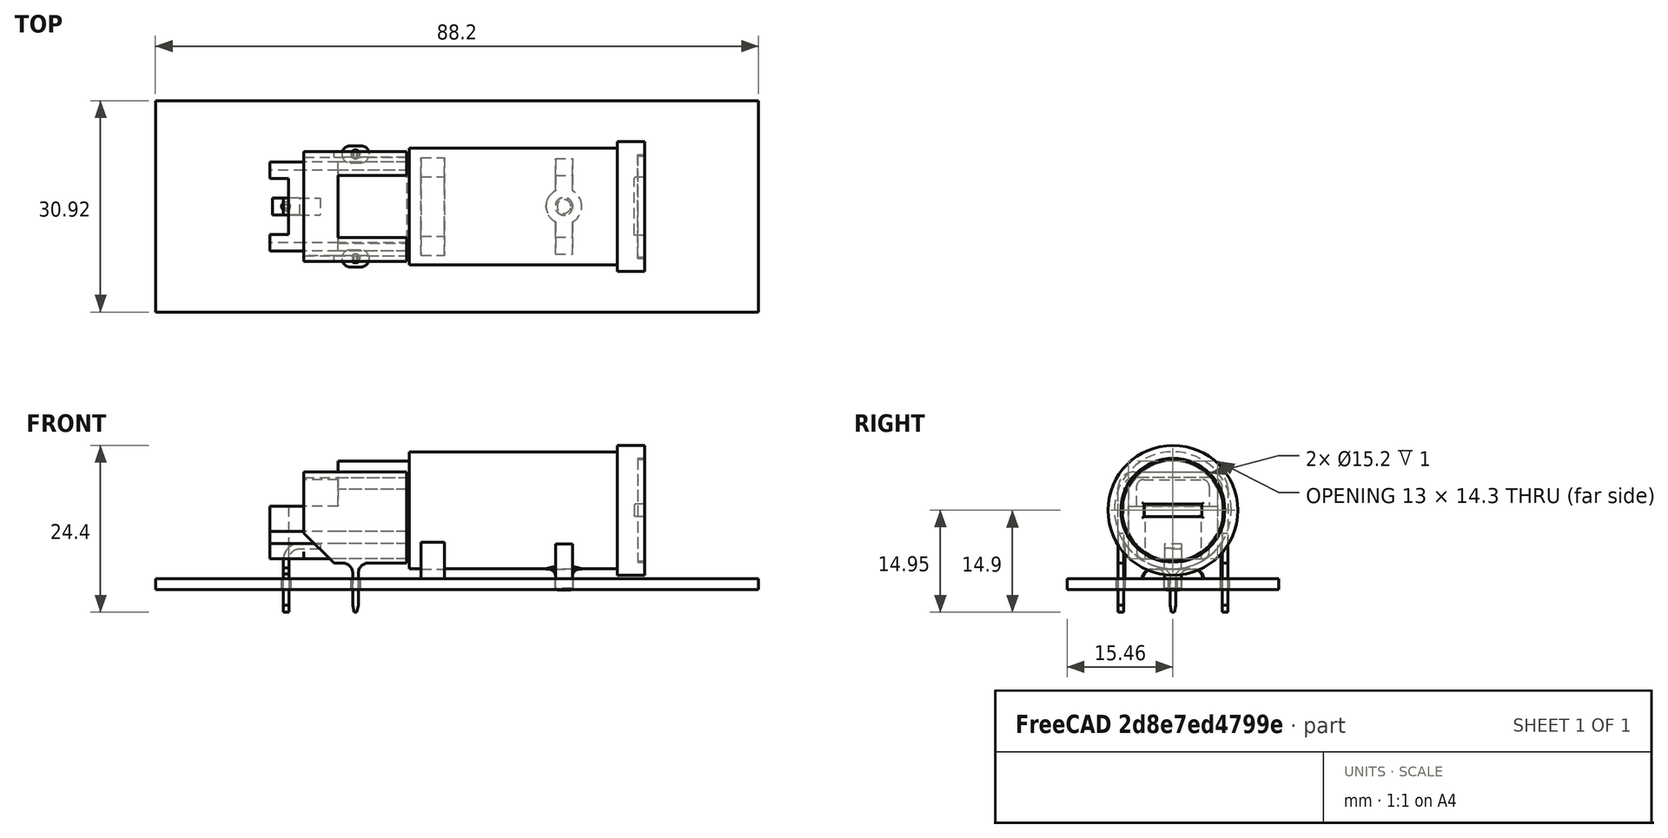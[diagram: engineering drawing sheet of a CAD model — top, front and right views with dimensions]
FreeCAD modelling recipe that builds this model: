
FCSTD DOCUMENT  (FreeCAD 0.17R12320 (Git))
Label: Fuseholder_Cylinder-5x20mm-or-6.3x32mm_Schurter_FUP_0031.25x0_Horizontal_Closed
License: All rights reserved
LicenseURL: http://en.wikipedia.org/wiki/All_rights_reserved
objects: Sketcher::SketchObject×16, PartDesign::Pad×9, PartDesign::Pocket×5, Part::FeaturePython×5, PartDesign::Plane×4, PartDesign::Fillet×3, PartDesign::Body×3, PartDesign::Revolution×1, PartDesign::Chamfer×1, PartDesign::ShapeBinder×1, Part::MultiFuse×1, App::DocumentObjectGroup×1
note: 64 computed .brp shape members not serialized (recipe doc carries the construction recipe); baked Part::Feature solids carry a one-line shape summary decoded from their .brp

FEATURE [Sketcher::SketchObject] Sketch
  MapMode = 5
  Placement = pos=(0,0,0) rot=(1,0,0;1.5708rad)
  Support = -> [XZ_Plane]
  expr: Constraints[9] = 11.77 + 30.48 + 10.16
  sketch-geometry (5):
    g0: LineSegment [constr] StartX=-2.39 StartY=19.5 StartZ=0 EndX=52.41 EndY=19.5 EndZ=0
    g1: LineSegment [constr] StartX=52.41 StartY=19.5 StartZ=0 EndX=52.41 EndY=0.5 EndZ=0
    g2: LineSegment [constr] StartX=52.41 StartY=0.5 StartZ=0 EndX=-2.39 EndY=0.5 EndZ=0
    g3: LineSegment [constr] StartX=-2.39 StartY=0.5 StartZ=0 EndX=-2.39 EndY=19.5 EndZ=0
    g4: LineSegment StartX=52.41 StartY=10 StartZ=0 EndX=-2.39 EndY=10 EndZ=0
  constraints (16):
    c: Coincident(g0,g1)
    c: Coincident(g1,g2)
    c: Coincident(g2,g3)
    c: Coincident(g3,g0)
    c: Horizontal(g0)
    c: Horizontal(g2)
    c: Vertical(g1)
    c: Vertical(g3)
    c: DistanceX(g0,g0) = 54.8
    c: DistanceX(g-1,g1) = 52.41
    c: DistanceY(g3,g3) = 19
    c: PointOnObject(g4,g1)
    c: PointOnObject(g4,g3)
    c: Horizontal(g4)
    c: Symmetric(g1,g0,g4)
    c: DistanceY(g-1,g0) = 19.5
FEATURE [Sketcher::SketchObject] Sketch001
  ExternalGeometry = -> [Sketch]
  MapMode = 5
  Placement = pos=(0,0,0) rot=(1,0,0;1.5708rad)
  Support = -> [XZ_Plane]
  sketch-geometry (11):
    g0: LineSegment StartX=52.41 StartY=10 StartZ=0 EndX=52.41 EndY=19.5 EndZ=0
    g1: LineSegment StartX=52.41 StartY=19.5 StartZ=0 EndX=48.41 EndY=19.5 EndZ=0
    g2: LineSegment StartX=48.41 StartY=19.5 StartZ=0 EndX=48.41 EndY=18.55 EndZ=0
    g3: LineSegment StartX=48.41 StartY=18.55 StartZ=0 EndX=18.01 EndY=18.55 EndZ=0
    g4: LineSegment StartX=18.01 StartY=18.55 StartZ=0 EndX=18.01 EndY=10 EndZ=0
    g5: LineSegment StartX=18.01 StartY=10 StartZ=0 EndX=52.41 EndY=10 EndZ=0
    g6: LineSegment [constr] StartX=52.41 StartY=10 StartZ=0 EndX=52.41 EndY=0.5 EndZ=0
    g7: LineSegment [constr] StartX=52.41 StartY=0.5 StartZ=0 EndX=48.41 EndY=0.5 EndZ=0
    g8: LineSegment [constr] StartX=48.41 StartY=0.5 StartZ=0 EndX=48.41 EndY=1.45 EndZ=0
    g9: LineSegment [constr] StartX=48.41 StartY=1.45 StartZ=0 EndX=18.01 EndY=1.45 EndZ=0
    g10: LineSegment [constr] StartX=18.01 StartY=1.45 StartZ=0 EndX=18.01 EndY=10 EndZ=0
  constraints (30):
    c: Coincident(g-3,g0)
    c: Vertical(g0)
    c: Coincident(g0,g1)
    c: Horizontal(g1)
    c: Coincident(g1,g2)
    c: Vertical(g2)
    c: Coincident(g2,g3)
    c: Horizontal(g3)
    c: Coincident(g3,g4)
    c: PointOnObject(g5,g-3)
    c: Coincident(g5,g0)
    c: DistanceX(g3,g3) = 30.4
    c: Vertical(g4)
    c: DistanceX(g1,g1) = 4
    c: Coincident(g0,g6)
    c: Vertical(g6)
    c: Coincident(g6,g7)
    c: Horizontal(g7)
    c: Coincident(g7,g8)
    c: Vertical(g8)
    c: Coincident(g8,g9)
    c: Horizontal(g9)
    c: Coincident(g9,g10)
    c: Vertical(g10)
    c: Symmetric(g8,g2,g-3)
    c: Symmetric(g0,g6,g-3)
    c: DistanceY(g6,g0) = 19
    c: Coincident(g5,g4)
    c: DistanceY(g9,g3) = 17.1
    c: Coincident(g10,g4)
FEATURE [PartDesign::Revolution] Revolution
  Angle = 360
  Axis = (-1,0,0)
  Base = (52.41,0,10)
  Placement = pos=(0,0,0) rot=(1,0,0;1.5708rad)
  Profile = -> Sketch001
  ReferenceAxis = -> Sketch [Edge1]
  Reversed = true
FEATURE [Sketcher::SketchObject] Sketch002
  ExternalGeometry = -> [Revolution]
  MapMode = 5
  Placement = pos=(18.01,0,0) rot=(0.707107,0,-0.707107;3.14159rad)
  Support = -> [Revolution]
  sketch-geometry (13):
    g0: Circle [constr] CenterX=-10 CenterY=0 CenterZ=0 NormalX=0 NormalY=0 NormalZ=1 AngleXU=0 Radius=7.2
    g1: GeomPoint [constr] X=-18.55 Y=0 Z=0
    g2: GeomPoint [constr] X=-17.2 Y=0 Z=0
    g3: LineSegment StartX=-13.0968 StartY=6.5 StartZ=0 EndX=-6.90323 EndY=6.5 EndZ=0
    g4: LineSegment StartX=-13.0968 StartY=-6.5 StartZ=0 EndX=-6.90323 EndY=-6.5 EndZ=0
    g5: LineSegment StartX=-5.1266 StartY=5.3 StartZ=0 EndX=-3.9 EndY=5.3 EndZ=0
    g6: LineSegment StartX=-2.9 StartY=4.3 StartZ=0 EndX=-2.9 EndY=-4.3 EndZ=0
    g7: LineSegment StartX=-3.9 StartY=-5.3 StartZ=0 EndX=-5.1266 EndY=-5.3 EndZ=0
    g8: ArcOfCircle CenterX=-3.9 CenterY=4.3 CenterZ=0 NormalX=0 NormalY=0 NormalZ=1 AngleXU=0 Radius=1 StartAngle=0 EndAngle=1.5708
    g9: ArcOfCircle CenterX=-3.9 CenterY=-4.3 CenterZ=0 NormalX=0 NormalY=0 NormalZ=1 AngleXU=0 Radius=1 StartAngle=4.71239 EndAngle=6.28319
    g10: ArcOfCircle CenterX=-10 CenterY=0 CenterZ=0 NormalX=0 NormalY=0 NormalZ=1 AngleXU=0 Radius=7.2 StartAngle=2.01541 EndAngle=4.26778
    g11: ArcOfCircle CenterX=-10 CenterY=0 CenterZ=0 NormalX=0 NormalY=0 NormalZ=1 AngleXU=0 Radius=7.2 StartAngle=0.827307 EndAngle=1.12618
    g12: ArcOfCircle CenterX=-10 CenterY=0 CenterZ=0 NormalX=0 NormalY=0 NormalZ=1 AngleXU=0 Radius=7.2 StartAngle=5.157 EndAngle=5.45588
  constraints (38):
    c: Coincident(g0,g-3)
    c: PointOnObject(g1,g-3)
    c: PointOnObject(g2,g0)
    c: PointOnObject(g2,g-1)
    c: PointOnObject(g1,g-1)
    c: DistanceX(g1,g2) = 1.35
    c: PointOnObject(g3,g0)
    c: Horizontal(g3)
    c: PointOnObject(g4,g0)
    c: Horizontal(g4)
    c: Symmetric(g3,g4,g-1)
    c: DistanceY(g4,g3) = 13
    c: PointOnObject(g3,g0)
    c: DistanceX(g3,g3) = 6.19355
    c: PointOnObject(g4,g0)
    c: PointOnObject(g5,g0)
    c: Horizontal(g5)
    c: Vertical(g6)
    c: PointOnObject(g7,g0)
    c: Horizontal(g7)
    c: Symmetric(g5,g7,g-1)
    c: DistanceY(g7,g5) = 10.6
    c: Tangent(g6,g8) = 1.5708
    c: Tangent(g5,g8) = 1.5708
    c: Tangent(g6,g9) = 1.5708
    c: Tangent(g7,g9) = 1.5708
    c: Radius(g8) = 1
    c: Equal(g8,g9)
    c: Coincident(g10,g0)
    c: Coincident(g10,g3)
    c: Coincident(g10,g4)
    c: Coincident(g11,g0)
    c: Coincident(g11,g3)
    c: Coincident(g11,g5)
    c: Coincident(g12,g0)
    c: Coincident(g12,g4)
    c: Coincident(g12,g7)
    c: DistanceX(g6,g-1) = 2.9
FEATURE [PartDesign::Pad] Pad
  BaseFeature = -> Revolution
  Length = 10.4
  Length2 = 100
  Placement = pos=(0,0,0) rot=(1,0,0;1.5708rad)
  Profile = -> Sketch002
  Type = 0
FEATURE [Sketcher::SketchObject] Sketch003
  ExternalGeometry = -> [Pad]
  MapMode = 5
  Placement = pos=(7.61,0,0) rot=(0.707107,0,-0.707107;3.14159rad)
  Support = -> [Pad]
  sketch-geometry (16):
    g0: LineSegment StartX=-2.9 StartY=4.3 StartZ=0 EndX=-2.9 EndY=-4.3 EndZ=0
    g1: LineSegment StartX=-3.9 StartY=5.3 StartZ=0 EndX=-5.1266 EndY=5.3 EndZ=0
    g2: LineSegment StartX=-5.1266 StartY=-5.3 StartZ=0 EndX=-3.9 EndY=-5.3 EndZ=0
    g3: LineSegment StartX=-6.90323 StartY=6.5 StartZ=0 EndX=-10.5968 EndY=6.5 EndZ=0
    g4: LineSegment StartX=-10.5968 StartY=-6.5 StartZ=0 EndX=-6.90323 EndY=-6.5 EndZ=0
    g5: ArcOfCircle CenterX=-10 CenterY=0 CenterZ=0 NormalX=0 NormalY=0 NormalZ=1 AngleXU=0 Radius=7.2 StartAngle=0.827307 EndAngle=1.12618
    g6: ArcOfCircle CenterX=-10 CenterY=0 CenterZ=0 NormalX=0 NormalY=0 NormalZ=1 AngleXU=0 Radius=7.2 StartAngle=5.157 EndAngle=5.45588
    g7: LineSegment StartX=-10.5968 StartY=6.5 StartZ=0 EndX=-10.5968 EndY=5.3 EndZ=0
    g8: LineSegment StartX=-10.5968 StartY=5.3 StartZ=0 EndX=-13.4968 EndY=5.3 EndZ=0
    g9: LineSegment StartX=-14.4968 StartY=4.3 StartZ=0 EndX=-14.4968 EndY=-4.3 EndZ=0
    g10: LineSegment StartX=-13.4968 StartY=-5.3 StartZ=0 EndX=-10.5968 EndY=-5.3 EndZ=0
    g11: LineSegment StartX=-10.5968 StartY=-5.3 StartZ=0 EndX=-10.5968 EndY=-6.5 EndZ=0
    g12: ArcOfCircle CenterX=-13.4968 CenterY=-4.3 CenterZ=0 NormalX=0 NormalY=0 NormalZ=1 AngleXU=0 Radius=1 StartAngle=3.14159 EndAngle=4.71239
    g13: ArcOfCircle CenterX=-13.4968 CenterY=4.3 CenterZ=0 NormalX=0 NormalY=0 NormalZ=1 AngleXU=0 Radius=1 StartAngle=1.5708 EndAngle=3.14159
    g14: ArcOfCircle CenterX=-3.9 CenterY=4.3 CenterZ=0 NormalX=0 NormalY=0 NormalZ=1 AngleXU=0 Radius=1 StartAngle=9e-12 EndAngle=1.5708
    g15: ArcOfCircle CenterX=-3.9 CenterY=-4.3 CenterZ=0 NormalX=0 NormalY=0 NormalZ=1 AngleXU=0 Radius=1 StartAngle=4.71239 EndAngle=6.28319
  constraints (41):
    c: Coincident(g0,g-8)
    c: Coincident(g0,g-8)
    c: Coincident(g1,g-7)
    c: Coincident(g1,g-7)
    c: Coincident(g2,g-6)
    c: Coincident(g2,g-6)
    c: Coincident(g-4,g3)
    c: PointOnObject(g3,g-4)
    c: Coincident(g4,g-5)
    c: Coincident(g5,g-3)
    c: Coincident(g5,g3)
    c: Coincident(g5,g1)
    c: Coincident(g6,g5)
    c: Coincident(g6,g2)
    c: Coincident(g6,g4)
    c: Coincident(g3,g7)
    c: Vertical(g7)
    c: Coincident(g7,g8)
    c: Horizontal(g8)
    c: Vertical(g9)
    c: Horizontal(g10)
    c: Coincident(g10,g11)
    c: Coincident(g11,g4)
    c: Vertical(g11)
    c: Symmetric(g10,g7,g-1)
    c: DistanceX(g-5,g4) = 2.5
    c: DistanceY(g11,g11) = 1.2
    c: Tangent(g9,g12) = -1.5708
    c: Tangent(g10,g12) = -1.5708
    c: Tangent(g9,g13) = -1.5708
    c: Tangent(g8,g13) = -1.5708
    c: DistanceX(g9,g10) = 3.9
    c: PointOnObject(g4,g-5)
    c: Radius(g12) = 1
    c: Equal(g12,g13)
    c: Coincident(g14,g0)
    c: Coincident(g14,g1)
    c: Coincident(g15,g0)
    c: Coincident(g15,g2)
    c: Equal(g-9,g15)
    c: Equal(g14,g-10)
FEATURE [PartDesign::Pad] Pad001
  BaseFeature = -> Pad
  Length = 5
  Length2 = 100
  Placement = pos=(0,0,0) rot=(1,0,0;1.5708rad)
  Profile = -> Sketch003
  Type = 0
FEATURE [Sketcher::SketchObject] Sketch004
  ExternalGeometry = -> [Pad001]
  MapMode = 5
  Placement = pos=(2.61,0,0) rot=(0.707107,0,-0.707107;3.14159rad)
  Support = -> [Pad001]
  sketch-geometry (10):
    g0: LineSegment StartX=-10.5968 StartY=6.5 StartZ=0 EndX=-6.90323 EndY=6.5 EndZ=0
    g1: LineSegment StartX=-10.5968 StartY=-6.5 StartZ=0 EndX=-6.90323 EndY=-6.5 EndZ=0
    g2: LineSegment StartX=-5.1266 StartY=5.3 StartZ=0 EndX=-3.9 EndY=5.3 EndZ=0
    g3: LineSegment StartX=-5.1266 StartY=-5.3 StartZ=0 EndX=-3.9 EndY=-5.3 EndZ=0
    g4: LineSegment StartX=-2.9 StartY=4.3 StartZ=0 EndX=-2.9 EndY=-4.3 EndZ=0
    g5: LineSegment StartX=-10.5968 StartY=6.5 StartZ=0 EndX=-10.5968 EndY=-6.5 EndZ=0
    g6: ArcOfCircle CenterX=-3.89999 CenterY=4.30001 CenterZ=0 NormalX=0 NormalY=0 NormalZ=1 AngleXU=0 Radius=0.99999 StartAngle=6.28318 EndAngle=7.85399
    g7: ArcOfCircle CenterX=-3.89999 CenterY=-4.30001 CenterZ=0 NormalX=0 NormalY=0 NormalZ=1 AngleXU=0 Radius=0.999991 StartAngle=4.71238 EndAngle=6.28319
    g8: ArcOfCircle CenterX=-10 CenterY=0 CenterZ=0 NormalX=0 NormalY=0 NormalZ=1 AngleXU=0 Radius=7.2 StartAngle=0.827307 EndAngle=1.12618
    g9: ArcOfCircle CenterX=-10 CenterY=0 CenterZ=0 NormalX=0 NormalY=0 NormalZ=1 AngleXU=0 Radius=7.2 StartAngle=5.157 EndAngle=5.45588
  constraints (24):
    c: Coincident(g5,g0)
    c: Coincident(g1,g5)
    c: Coincident(g4,g-7)
    c: Coincident(g4,g-7)
    c: Coincident(g2,g-6)
    c: Coincident(g2,g-6)
    c: Coincident(g0,g-3)
    c: Coincident(g0,g-3)
    c: Coincident(g1,g-4)
    c: Coincident(g1,g-4)
    c: Coincident(g3,g-5)
    c: Coincident(g3,g-5)
    c: Coincident(g6,g2)
    c: Coincident(g6,g4)
    c: Tangent(g6,g-6)
    c: Coincident(g7,g4)
    c: Coincident(g7,g3)
    c: Tangent(g-7,g7)
    c: Coincident(g8,g0)
    c: Coincident(g8,g2)
    c: Coincident(g9,g1)
    c: Coincident(g9,g3)
    c: Equal(g-9,g9)
    c: Equal(g8,g-8)
FEATURE [PartDesign::Pad] Pad002
  BaseFeature = -> Pad001
  Length = 5
  Length2 = 100
  Placement = pos=(0,0,0) rot=(1,0,0;1.5708rad)
  Profile = -> Sketch004
  Type = 0
FEATURE [Sketcher::SketchObject] Sketch005
  ExternalGeometry = -> [Pad002]
  MapMode = 5
  Placement = pos=(0,0,10.5968) rot=(0,0,1;3.14159rad)
  Support = -> [Pad002]
  sketch-geometry (4):
    g0: LineSegment StartX=-0.35 StartY=4.1 StartZ=0 EndX=2.39 EndY=4.1 EndZ=0
    g1: LineSegment StartX=2.39 StartY=4.1 StartZ=0 EndX=2.39 EndY=-4.1 EndZ=0
    g2: LineSegment StartX=2.39 StartY=-4.1 StartZ=0 EndX=-0.35 EndY=-4.1 EndZ=0
    g3: LineSegment StartX=-0.35 StartY=-4.1 StartZ=0 EndX=-0.35 EndY=4.1 EndZ=0
  constraints (12):
    c: Coincident(g0,g1)
    c: Coincident(g1,g2)
    c: Coincident(g2,g3)
    c: Coincident(g3,g0)
    c: Horizontal(g0)
    c: Horizontal(g2)
    c: Vertical(g1)
    c: Vertical(g3)
    c: PointOnObject(g1,g-3)
    c: Symmetric(g0,g1,g-1)
    c: DistanceY(g3,g3) = 8.2
    c: DistanceX(g0,g0) = 2.74
FEATURE [PartDesign::Pocket] Pocket
  BaseFeature = -> Pad002
  Length = 5
  Placement = pos=(0,0,0) rot=(1,0,0;1.5708rad)
  Profile = -> Sketch005
  Type = 1
FEATURE [PartDesign::Plane] DatumPlane
  MapMode = 5
  Placement = pos=(19.74,0,0) rot=(0.707107,0,-0.707107;3.14159rad)
  Support = -> [Revolution]
  superPlacement = pos=(0,0,32.67) rot=(0,0,1;0rad)
FEATURE [PartDesign::Plane] DatumPlane001
  MapMode = 5
  Placement = pos=(39.39,0,0) rot=(0.707107,0,-0.707107;3.14159rad)
  Support = -> [Revolution]
  superPlacement = pos=(0,0,13.02) rot=(0,0,1;0rad)
FEATURE [Sketcher::SketchObject] Sketch006
  ExternalGeometry = -> [Pocket]
  MapMode = 5
  Placement = pos=(19.74,0,0) rot=(0.707107,0,-0.707107;3.14159rad)
  Support = -> [DatumPlane]
  sketch-geometry (8):
    g0: LineSegment StartX=-5.31172 StartY=7.15 StartZ=0 EndX=0 EndY=7.15 EndZ=0
    g1: LineSegment StartX=0 StartY=7.15 StartZ=0 EndX=0 EndY=4.35 EndZ=0
    g2: LineSegment StartX=-1.4 StartY=2.95002 StartZ=0 EndX=-1.4 EndY=-2.95002 EndZ=0
    g3: LineSegment StartX=0 StartY=-4.35 StartZ=0 EndX=0 EndY=-7.15 EndZ=0
    g4: LineSegment StartX=0 StartY=-7.15 StartZ=0 EndX=-5.31172 EndY=-7.15 EndZ=0
    g5: LineSegment StartX=-5.31172 StartY=-7.15 StartZ=0 EndX=-5.31172 EndY=7.15 EndZ=0
    g6: ArcOfCircle CenterX=0 CenterY=2.95 CenterZ=0 NormalX=0 NormalY=0 NormalZ=1 AngleXU=0 Radius=1.4 StartAngle=1.5708 EndAngle=3.14158
    g7: ArcOfCircle CenterX=0 CenterY=-2.95 CenterZ=0 NormalX=0 NormalY=0 NormalZ=1 AngleXU=0 Radius=1.4 StartAngle=3.1416 EndAngle=4.71239
  constraints (25):
    c: PointOnObject(g0,g-3)
    c: PointOnObject(g0,g-2)
    c: Horizontal(g0)
    c: Coincident(g0,g1)
    c: PointOnObject(g1,g-2)
    c: Vertical(g3)
    c: Coincident(g3,g4)
    c: PointOnObject(g4,g-3)
    c: Horizontal(g4)
    c: Coincident(g4,g5)
    c: Coincident(g5,g0)
    c: Vertical(g5)
    c: Symmetric(g1,g3,g-1)
    c: Symmetric(g2,g2,g-1)
    c: DistanceX(g2,g1) = 1.4
    c: DistanceY(g3,g0) = 14.3
    c: DistanceY(g3,g1) = 8.7
    c: PointOnObject(g6,g-2)
    c: Coincident(g6,g2)
    c: Coincident(g6,g1)
    c: Coincident(g7,g2)
    c: PointOnObject(g7,g-2)
    c: Tangent(g7,g2)
    c: Tangent(g6,g2)
    c: Coincident(g3,g7)
FEATURE [PartDesign::Pad] Pad003
  BaseFeature = -> Pocket
  Length = 3.4
  Length2 = 100
  Placement = pos=(0,0,0) rot=(1,0,0;1.5708rad)
  Profile = -> Sketch006
  Reversed = true
  Type = 0
FEATURE [Sketcher::SketchObject] Sketch007
  ExternalGeometry = -> [Pad003]
  MapMode = 5
  Placement = pos=(39.39,0,0) rot=(0.707107,0,-0.707107;3.14159rad)
  Support = -> [DatumPlane001]
  sketch-geometry (8):
    g0: LineSegment StartX=-5.09057 StartY=7 StartZ=0 EndX=0 EndY=7 EndZ=0
    g1: LineSegment StartX=0 StartY=7 StartZ=0 EndX=0 EndY=4.5 EndZ=0
    g2: LineSegment StartX=-1.4 StartY=3.1 StartZ=0 EndX=-1.4 EndY=-3.1 EndZ=0
    g3: LineSegment StartX=0 StartY=-4.5 StartZ=0 EndX=0 EndY=-7 EndZ=0
    g4: LineSegment StartX=0 StartY=-7 StartZ=0 EndX=-5.09057 EndY=-7 EndZ=0
    g5: LineSegment StartX=-5.09057 StartY=-7 StartZ=0 EndX=-5.09057 EndY=7 EndZ=0
    g6: ArcOfCircle CenterX=0 CenterY=3.1 CenterZ=0 NormalX=0 NormalY=0 NormalZ=1 AngleXU=0 Radius=1.4 StartAngle=1.5708 EndAngle=3.14159
    g7: ArcOfCircle CenterX=0 CenterY=-3.1 CenterZ=0 NormalX=0 NormalY=0 NormalZ=1 AngleXU=0 Radius=1.4 StartAngle=3.14159 EndAngle=4.71239
  constraints (26):
    c: PointOnObject(g0,g-3)
    c: Horizontal(g0)
    c: Coincident(g0,g1)
    c: PointOnObject(g1,g-2)
    c: Vertical(g2)
    c: PointOnObject(g3,g-2)
    c: Vertical(g3)
    c: Coincident(g3,g4)
    c: PointOnObject(g4,g-3)
    c: Horizontal(g4)
    c: Coincident(g4,g5)
    c: Coincident(g5,g0)
    c: Vertical(g5)
    c: DistanceY(g3,g0) = 14
    c: DistanceY(g3,g1) = 9
    c: PointOnObject(g6,g-2)
    c: Coincident(g6,g2)
    c: Coincident(g6,g1)
    c: Symmetric(g1,g3,g-1)
    c: Tangent(g6,g2)
    c: PointOnObject(g7,g-2)
    c: Coincident(g7,g2)
    c: Coincident(g7,g3)
    c: Tangent(g2,g7)
    c: Radius(g7) = 1.4
    c: Vertical(g1)
FEATURE [PartDesign::Plane] DatumPlane002
  MapMode = 5
  Placement = pos=(0,0,1.4) rot=(0,0,1;0rad)
  Support = -> [XY_Plane]
  superPlacement = pos=(0,0,1.4) rot=(0,0,1;0rad)
FEATURE [Sketcher::SketchObject] Sketch008
  ExternalGeometry = -> [Sketch]
  MapMode = 5
  Placement = pos=(0,0,1.4) rot=(0,0,1;0rad)
  Support = -> [DatumPlane002]
  expr: Constraints[2] = 10.16 + 30.48
  expr: Constraints[1] = 5.2000000000000002 / 2
  sketch-geometry (1):
    g0: Circle CenterX=40.64 CenterY=0 CenterZ=0 NormalX=0 NormalY=0 NormalZ=1 AngleXU=0 Radius=2.6
  constraints (3):
    c: PointOnObject(g0,g-1)
    c: Radius(g0) = 2.6
    c: DistanceX(g-1,g0) = 40.64
FEATURE [PartDesign::Pad] Pad004
  BaseFeature = -> Pad003
  Length = 1
  Length2 = 100
  Placement = pos=(0,0,0) rot=(1,0,0;1.5708rad)
  Profile = -> Sketch008
  Type = 0
FEATURE [Sketcher::SketchObject] Sketch009
  ExternalGeometry = -> [Pad004]
  MapMode = 5
  Placement = pos=(0,0,1.4) rot=(1,0,0;3.14159rad)
  Support = -> [Pad004]
  expr: Constraints[1] = 2.5 / 2
  sketch-geometry (1):
    g0: Circle CenterX=40.64 CenterY=0 CenterZ=0 NormalX=0 NormalY=0 NormalZ=1 AngleXU=0 Radius=1.25
  constraints (2):
    c: Coincident(g0,g-3)
    c: Radius(g0) = 1.25
FEATURE [PartDesign::Pad] Pad005
  BaseFeature = -> Pad004
  Length = 3.04
  Length2 = 100
  Placement = pos=(0,0,0) rot=(1,0,0;1.5708rad)
  Profile = -> Sketch009
  Type = 0
  expr: Length = 1.4399999999999999 + 1.6000000000000001
FEATURE [PartDesign::Fillet] Fillet
  Base = -> Pad005 [Edge65]
  BaseFeature = -> Pad005
  Placement = pos=(0,0,0) rot=(1,0,0;1.5708rad)
  Radius = 1
FEATURE [PartDesign::Chamfer] Chamfer
  Base = -> Fillet [Edge11]
  BaseFeature = -> Fillet
  Placement = pos=(0,0,0) rot=(1,0,0;1.5708rad)
  Size = 0.25
FEATURE [PartDesign::Pad] Pad006
  BaseFeature = -> Chamfer
  Length = 2.5
  Length2 = 100
  Placement = pos=(0,0,0) rot=(1,0,0;1.5708rad)
  Profile = -> Sketch007
  Reversed = true
  Type = 0
FEATURE [Sketcher::SketchObject] Sketch010
  ExternalGeometry = -> [Pad006]
  MapMode = 5
  Placement = pos=(52.41,0,0) rot=(0.707107,0,0.707107;3.14159rad)
  Support = -> [Pad006]
  sketch-geometry (2):
    g0: Circle CenterX=10 CenterY=0 CenterZ=0 NormalX=0 NormalY=0 NormalZ=1 AngleXU=0 Radius=7.6
    g1: Circle CenterX=10 CenterY=0 CenterZ=0 NormalX=0 NormalY=0 NormalZ=1 AngleXU=0 Radius=7.4
  constraints (2):
    c: Radius(g0) = 7.6
    c: Radius(g1) = 7.4
FEATURE [PartDesign::Pocket] Pocket001
  BaseFeature = -> Pad006
  Length = 1
  Placement = pos=(0,0,0) rot=(1,0,0;1.5708rad)
  Profile = -> Sketch010
  Type = 0
FEATURE [Sketcher::SketchObject] Sketch011
  ExternalGeometry = -> [Pocket001]
  MapMode = 5
  Placement = pos=(52.41,0,0) rot=(0.707107,0,0.707107;3.14159rad)
  Support = -> [Pocket001]
  sketch-geometry (5):
    g0: LineSegment StartX=9.1 StartY=4.25 StartZ=0 EndX=10.9 EndY=4.25 EndZ=0
    g1: LineSegment StartX=10.9 StartY=4.25 StartZ=0 EndX=10.9 EndY=-4.25 EndZ=0
    g2: LineSegment StartX=10.9 StartY=-4.25 StartZ=0 EndX=9.1 EndY=-4.25 EndZ=0
    g3: LineSegment StartX=9.1 StartY=-4.25 StartZ=0 EndX=9.1 EndY=4.25 EndZ=0
    g4: LineSegment [constr] StartX=10 StartY=4.25 StartZ=0 EndX=10 EndY=-4.25 EndZ=0
  constraints (16):
    c: Coincident(g0,g1)
    c: Coincident(g1,g2)
    c: Coincident(g2,g3)
    c: Coincident(g3,g0)
    c: Horizontal(g0)
    c: Horizontal(g2)
    c: Vertical(g1)
    c: Vertical(g3)
    c: PointOnObject(g4,g0)
    c: PointOnObject(g4,g2)
    c: Vertical(g4)
    c: PointOnObject(g-3,g4)
    c: Symmetric(g4,g4,g-1)
    c: Symmetric(g0,g0,g4)
    c: DistanceX(g0,g0) = 1.8
    c: DistanceY(g1,g1) = 8.5
FEATURE [PartDesign::Pocket] Pocket002
  BaseFeature = -> Pocket001
  Length = 1.5
  Placement = pos=(0,0,0) rot=(1,0,0;1.5708rad)
  Profile = -> Sketch011
  Type = 0
FEATURE [PartDesign::Fillet] Fillet001
  Base = -> Pocket002 [Edge207,Edge201,Edge200,Edge205,Edge202,Edge209,Edge211,Edge203]
  BaseFeature = -> Pocket002
  Placement = pos=(0,0,0) rot=(1,0,0;1.5708rad)
  Radius = 0.2
FEATURE [PartDesign::Fillet] Fillet002
  Base = -> Fillet001 [Edge5]
  BaseFeature = -> Fillet001
  Placement = pos=(0,0,0) rot=(1,0,0;1.5708rad)
  Radius = 0.25
FEATURE [PartDesign::Body] Body
  Origin = -> BodyOrigin
  Tip = -> Fillet002
FEATURE [PartDesign::ShapeBinder] CopyFillet002
  Placement = pos=(0,0,0) rot=(1,0,0;1.5708rad)
FEATURE [PartDesign::Plane] DatumPlane003
  MapMode = 5
  Placement = pos=(2.61,0,0) rot=(0.707107,0,-0.707107;3.14159rad)
  Support = -> [CopyFillet002]
FEATURE [Sketcher::SketchObject] Sketch012
  MapMode = 5
  Placement = pos=(2.61,0,0) rot=(0.707107,0,-0.707107;3.14159rad)
  Support = -> [DatumPlane003]
  expr: Constraints[1] = 19 / 2
  sketch-geometry (17):
    g0: Circle [constr] CenterX=-10 CenterY=0 CenterZ=0 NormalX=0 NormalY=0 NormalZ=1 AngleXU=0 Radius=9.5
    g1: GeomPoint [constr] X=-19.5 Y=0 Z=0
    g2: LineSegment [constr] StartX=4.9 StartY=7.62 StartZ=0 EndX=-15.2 EndY=7.62 EndZ=0
    g3: LineSegment [constr] StartX=-15.2 StartY=7.62 StartZ=0 EndX=-15.2 EndY=-7.62 EndZ=0
    g4: LineSegment [constr] StartX=-15.2 StartY=-7.62 StartZ=0 EndX=4.9 EndY=-7.62 EndZ=0
    g5: LineSegment StartX=4.9 StartY=7.22 StartZ=0 EndX=4.9 EndY=8.02 EndZ=0
    g6: LineSegment StartX=4.9 StartY=8.02 StartZ=0 EndX=-13.3 EndY=8.02 EndZ=0
    g7: LineSegment StartX=-15.6 StartY=5.72 StartZ=0 EndX=-15.6 EndY=-5.72 EndZ=0
    g8: LineSegment StartX=-13.3 StartY=-8.02 StartZ=0 EndX=4.9 EndY=-8.02 EndZ=0
    g9: LineSegment StartX=4.9 StartY=-8.02 StartZ=0 EndX=4.9 EndY=-7.22 EndZ=0
    g10: LineSegment StartX=4.9 StartY=-7.22 StartZ=0 EndX=-13.3 EndY=-7.22 EndZ=0
    g11: LineSegment StartX=-14.8 StartY=-5.72 StartZ=0 EndX=-14.8 EndY=5.72 EndZ=0
    g12: LineSegment StartX=-13.3 StartY=7.22 StartZ=0 EndX=4.9 EndY=7.22 EndZ=0
    g13: ArcOfCircle CenterX=-13.3 CenterY=5.72 CenterZ=0 NormalX=0 NormalY=0 NormalZ=1 AngleXU=0 Radius=1.5 StartAngle=1.5708 EndAngle=3.14159
    g14: ArcOfCircle CenterX=-13.3 CenterY=5.72 CenterZ=0 NormalX=0 NormalY=0 NormalZ=1 AngleXU=0 Radius=2.3 StartAngle=1.5708 EndAngle=3.14159
    g15: ArcOfCircle CenterX=-13.3 CenterY=-5.72 CenterZ=0 NormalX=0 NormalY=0 NormalZ=1 AngleXU=0 Radius=1.5 StartAngle=3.14159 EndAngle=4.71239
    g16: ArcOfCircle CenterX=-13.3 CenterY=-5.72 CenterZ=0 NormalX=0 NormalY=0 NormalZ=1 AngleXU=0 Radius=2.3 StartAngle=3.14159 EndAngle=4.71239
  constraints (45):
    c: PointOnObject(g0,g-1)
    c: Radius(g0) = 9.5
    c: PointOnObject(g1,g0)
    c: PointOnObject(g1,g-1)
    c: DistanceX(g1,g-1) = 19.5
    c: Horizontal(g2)
    c: Coincident(g2,g3)
    c: Vertical(g3)
    c: Coincident(g3,g4)
    c: Horizontal(g4)
    c: Symmetric(g2,g4,g-1)
    c: DistanceX(g0,g2) = 14.9
    c: DistanceY(g3,g3) = 15.24
    c: DistanceX(g2,g2) = 20.1
    c: Coincident(g5,g6)
    c: Horizontal(g6)
    c: Vertical(g7)
    c: Horizontal(g8)
    c: Coincident(g8,g9)
    c: Vertical(g9)
    c: Horizontal(g10)
    c: Vertical(g11)
    c: Coincident(g12,g5)
    c: Horizontal(g12)
    c: Vertical(g5)
    c: PointOnObject(g2,g5)
    c: PointOnObject(g4,g9)
    c: Tangent(g12,g13) = 1.5708
    c: Tangent(g11,g13) = 1.5708
    c: Tangent(g6,g14) = -1.5708
    c: Tangent(g7,g14) = -1.5708
    c: Tangent(g10,g15) = 1.5708
    c: Tangent(g11,g15) = 1.5708
    c: Tangent(g8,g16) = -1.5708
    c: Tangent(g7,g16) = -1.5708
    c: Coincident(g13,g14)
    c: DistanceY(g5,g5) = 0.8
    c: Symmetric(g5,g5,g2)
    c: Coincident(g9,g10)
    c: Symmetric(g9,g8,g4)
    c: Coincident(g16,g15)
    c: Symmetric(g11,g7,g3)
    c: Radius(g13) = 1.5
    c: Equal(g13,g15)
    c: DistanceX(g-1,g4) = 4.9
FEATURE [PartDesign::Pad] Pad007
  Length = 15
  Length2 = 100
  Placement = pos=(2.61,0,0) rot=(0.707107,0,-0.707107;3.14159rad)
  Profile = -> Sketch012
  Reversed = true
  Type = 0
FEATURE [Sketcher::SketchObject] Sketch013
  ExternalGeometry = -> [Pad007]
  MapMode = 5
  Placement = pos=(0,0,0) rot=(1,0,0;1.5708rad)
  Support = -> [XZ_Plane001]
  sketch-geometry (15):
    g0: LineSegment [constr] StartX=10.16 StartY=-4.9 StartZ=0 EndX=10.16 EndY=13.3 EndZ=0
    g1: LineSegment StartX=9.96 StartY=-4.9 StartZ=0 EndX=9.76 EndY=-3.9 EndZ=0
    g2: LineSegment StartX=9.76 StartY=-3.9 StartZ=0 EndX=9.76 EndY=0.78 EndZ=0
    g3: LineSegment StartX=2.61 StartY=6.68 StartZ=0 EndX=2.11 EndY=6.68 EndZ=0
    g4: LineSegment StartX=2.11 StartY=6.68 StartZ=0 EndX=2.11 EndY=-5.4 EndZ=0
    g5: LineSegment StartX=2.11 StartY=-5.4 StartZ=0 EndX=18.11 EndY=-5.4 EndZ=0
    g6: LineSegment StartX=18.11 StartY=-5.4 StartZ=0 EndX=18.11 EndY=2.28 EndZ=0
    g7: LineSegment StartX=18.11 StartY=2.28 StartZ=0 EndX=12.06 EndY=2.28 EndZ=0
    g8: LineSegment StartX=10.56 StartY=0.78 StartZ=0 EndX=10.56 EndY=-3.9 EndZ=0
    g9: LineSegment StartX=10.56 StartY=-3.9 StartZ=0 EndX=10.36 EndY=-4.9 EndZ=0
    g10: LineSegment StartX=10.36 StartY=-4.9 StartZ=0 EndX=9.96 EndY=-4.9 EndZ=0
    g11: LineSegment StartX=2.61 StartY=6.68 StartZ=0 EndX=7.01 EndY=2.28 EndZ=0
    g12: LineSegment StartX=7.01 StartY=2.28 StartZ=0 EndX=8.26 EndY=2.28 EndZ=0
    g13: ArcOfCircle CenterX=8.26 CenterY=0.78 CenterZ=0 NormalX=0 NormalY=0 NormalZ=1 AngleXU=0 Radius=1.5 StartAngle=0 EndAngle=1.5708
    g14: ArcOfCircle CenterX=12.06 CenterY=0.78 CenterZ=0 NormalX=0 NormalY=0 NormalZ=1 AngleXU=0 Radius=1.5 StartAngle=1.5708 EndAngle=3.14159
  constraints (44):
    c: PointOnObject(g0,g-3)
    c: Vertical(g0)
    c: Equal(g0,g-5)
    c: DistanceX(g-1,g0) = 10.16
    c: PointOnObject(g1,g-3)
    c: Coincident(g1,g2)
    c: Vertical(g2)
    c: PointOnObject(g3,g-4)
    c: Horizontal(g3)
    c: Coincident(g3,g4)
    c: Vertical(g4)
    c: Coincident(g4,g5)
    c: Horizontal(g5)
    c: Coincident(g5,g6)
    c: Vertical(g6)
    c: Coincident(g6,g7)
    c: Horizontal(g7)
    c: Vertical(g8)
    c: Coincident(g8,g9)
    c: PointOnObject(g9,g-3)
    c: Coincident(g9,g10)
    c: Coincident(g10,g1)
    c: Coincident(g3,g11)
    c: Coincident(g11,g12)
    c: Horizontal(g12)
    c: Tangent(g12,g13) = 1.5708
    c: Tangent(g2,g13) = -1.5708
    c: Tangent(g7,g14) = -1.5708
    c: Tangent(g8,g14) = -1.5708
    c: Symmetric(g8,g1,g0)
    c: Symmetric(g8,g2,g0)
    c: DistanceX(g1,g8) = 0.8
    c: Symmetric(g1,g9,g0)
    c: DistanceY(g9,g8) = 1
    c: DistanceX(g9,g9) = 0.2
    c: DistanceY(g-5,g6) = 7.18
    c: PointOnObject(g12,g7)
    c: Radius(g14) = 1.5
    c: Equal(g14,g13)
    c: DistanceY(g11,g11) = 4.4
    c: DistanceX(g11,g11) = 4.4
    c: DistanceX(g3,g3) = 0.5
    c: DistanceY(g4,g-4) = 0.5
    c: DistanceX(g-5,g5) = 0.5
FEATURE [PartDesign::Pocket] Pocket003
  BaseFeature = -> Pad007
  Length = 5
  Midplane = true
  Placement = pos=(2.61,0,0) rot=(0.707107,0,-0.707107;3.14159rad)
  Profile = -> Sketch013
  Type = 1
FEATURE [PartDesign::Body] Body001
  Origin = -> Body001Origin
  Tip = -> Pocket003
FEATURE [Sketcher::SketchObject] Sketch014
  MapMode = 5
  Placement = pos=(0,0,0) rot=(1,0,0;1.5708rad)
  Support = -> [XZ_Plane002]
  expr: Constraints[5] = 10 - 0.80000000000000004 / 2
  sketch-geometry (10):
    g0: LineSegment [constr] StartX=0 StartY=-4.9 StartZ=0 EndX=0 EndY=4.7 EndZ=0
    g1: LineSegment [constr] StartX=0 StartY=4.7 StartZ=0 EndX=5 EndY=4.7 EndZ=0
    g2: LineSegment StartX=-0.4 StartY=-4.9 StartZ=0 EndX=-0.4 EndY=2.8 EndZ=0
    g3: LineSegment StartX=1.9 StartY=5.1 StartZ=0 EndX=5 EndY=5.1 EndZ=0
    g4: LineSegment StartX=5 StartY=5.1 StartZ=0 EndX=5 EndY=4.3 EndZ=0
    g5: LineSegment StartX=5 StartY=4.3 StartZ=0 EndX=1.9 EndY=4.3 EndZ=0
    g6: LineSegment StartX=0.4 StartY=2.8 StartZ=0 EndX=0.4 EndY=-4.9 EndZ=0
    g7: LineSegment StartX=0.4 StartY=-4.9 StartZ=0 EndX=-0.4 EndY=-4.9 EndZ=0
    g8: ArcOfCircle CenterX=1.9 CenterY=2.8 CenterZ=0 NormalX=0 NormalY=0 NormalZ=1 AngleXU=0 Radius=1.5 StartAngle=1.5708 EndAngle=3.14159
    g9: ArcOfCircle CenterX=1.9 CenterY=2.8 CenterZ=0 NormalX=0 NormalY=0 NormalZ=1 AngleXU=0 Radius=2.3 StartAngle=1.5708 EndAngle=3.14159
  constraints (28):
    c: PointOnObject(g0,g-2)
    c: PointOnObject(g0,g-2)
    c: Coincident(g0,g1)
    c: Horizontal(g1)
    c: DistanceY(g0,g-1) = 4.9
    c: DistanceY(g0,g0) = 9.6
    c: DistanceX(g1,g1) = 5
    c: Vertical(g2)
    c: Horizontal(g3)
    c: Coincident(g3,g4)
    c: Vertical(g4)
    c: Coincident(g4,g5)
    c: Horizontal(g5)
    c: Vertical(g6)
    c: Coincident(g6,g7)
    c: Coincident(g7,g2)
    c: Horizontal(g7)
    c: Tangent(g5,g8) = -1.5708
    c: Tangent(g6,g8) = -1.5708
    c: Tangent(g3,g9) = 1.5708
    c: Tangent(g2,g9) = 1.5708
    c: Coincident(g9,g8)
    c: DistanceY(g4,g4) = 0.8
    c: PointOnObject(g1,g4)
    c: Symmetric(g3,g4,g1)
    c: Symmetric(g6,g2,g0)
    c: PointOnObject(g0,g7)
    c: Radius(g8) = 1.5
FEATURE [PartDesign::Pad] Pad008
  Length = 2.5
  Length2 = 100
  Midplane = true
  Placement = pos=(0,0,0) rot=(1,0,0;1.5708rad)
  Profile = -> Sketch014
  Type = 0
FEATURE [Sketcher::SketchObject] Sketch015
  ExternalGeometry = -> [Pad008]
  MapMode = 5
  Placement = pos=(-0.4,0,0) rot=(0.707107,0,-0.707107;3.14159rad)
  Support = -> [Pad008]
  sketch-geometry (12):
    g0: LineSegment StartX=4.9 StartY=0.2 StartZ=0 EndX=3.9 EndY=0.4 EndZ=0
    g1: LineSegment StartX=3.9 StartY=0.4 StartZ=0 EndX=-0.7 EndY=0.4 EndZ=0
    g2: LineSegment StartX=-0.7 StartY=0.4 StartZ=0 EndX=-1.55 EndY=1.25 EndZ=0
    g3: LineSegment StartX=-1.55 StartY=1.25 StartZ=0 EndX=-1.55 EndY=1.75 EndZ=0
    g4: LineSegment StartX=-1.55 StartY=1.75 StartZ=0 EndX=5.4 EndY=1.75 EndZ=0
    g5: LineSegment StartX=5.4 StartY=1.75 StartZ=0 EndX=5.4 EndY=-1.75 EndZ=0
    g6: LineSegment StartX=5.4 StartY=-1.75 StartZ=0 EndX=-1.55 EndY=-1.75 EndZ=0
    g7: LineSegment StartX=-1.55 StartY=-1.75 StartZ=0 EndX=-1.55 EndY=-1.25 EndZ=0
    g8: LineSegment StartX=-1.55 StartY=-1.25 StartZ=0 EndX=-0.7 EndY=-0.4 EndZ=0
    g9: LineSegment StartX=-0.7 StartY=-0.4 StartZ=0 EndX=3.9 EndY=-0.4 EndZ=0
    g10: LineSegment StartX=3.9 StartY=-0.4 StartZ=0 EndX=4.9 EndY=-0.2 EndZ=0
    g11: LineSegment StartX=4.9 StartY=-0.2 StartZ=0 EndX=4.9 EndY=0.2 EndZ=0
  constraints (35):
    c: PointOnObject(g0,g-4)
    c: Coincident(g0,g1)
    c: Horizontal(g1)
    c: Coincident(g1,g2)
    c: PointOnObject(g2,g-3)
    c: Coincident(g2,g3)
    c: Vertical(g3)
    c: Coincident(g3,g4)
    c: Horizontal(g4)
    c: Coincident(g4,g5)
    c: Vertical(g5)
    c: Coincident(g5,g6)
    c: Horizontal(g6)
    c: Coincident(g6,g7)
    c: PointOnObject(g7,g-5)
    c: Vertical(g7)
    c: Coincident(g7,g8)
    c: Coincident(g8,g9)
    c: Horizontal(g9)
    c: Coincident(g9,g10)
    c: PointOnObject(g10,g-4)
    c: Coincident(g10,g11)
    c: Coincident(g11,g0)
    c: Symmetric(g9,g0,g-1)
    c: Symmetric(g1,g8,g-1)
    c: PointOnObject(g2,g7)
    c: DistanceY(g9,g0) = 0.8
    c: DistanceX(g0,g0) = 1
    c: DistanceY(g0,g0) = 0.2
    c: Symmetric(g10,g0,g-1)
    c: DistanceX(g1,g0) = 5.6
    c: DistanceX(g2,g2) = 0.85
    c: DistanceY(g3,g3) = 0.5
    c: Symmetric(g4,g5,g-1)
    c: DistanceX(g-4,g4) = 0.5
FEATURE [PartDesign::Pocket] Pocket004
  BaseFeature = -> Pad008
  Length = 5
  Placement = pos=(0,0,0) rot=(1,0,0;1.5708rad)
  Profile = -> Sketch015
  Type = 1
FEATURE [PartDesign::Body] Body002
  Origin = -> Body002Origin
  Tip = -> Pocket004
FEATURE [Part::MultiFuse] Fusion  label="Fuseholder_Cylinder-5x20mm-or-6.3x32mm_Schurter_FUP_0031.25x0_Horizontal_Closed"
  Shapes = -> [Pocket004,Pocket003,Fillet002]
FEATURE [Part::FeaturePython] Filk_lines  label="FrontSilk"  # a2plus imported part (geometry in sourceFile) (typed FeaturePython)
  fixedPosition = true
FEATURE [Part::FeaturePython] TopPads  # a2plus imported part (geometry in sourceFile) (typed FeaturePython)
  fixedPosition = true
FEATURE [Part::FeaturePython] BotPads  # a2plus imported part (geometry in sourceFile) (typed FeaturePython)
  fixedPosition = true
FEATURE [Part::FeaturePython] THPs  label="PTHs"  # a2plus imported part (geometry in sourceFile) (typed FeaturePython)
  fixedPosition = true
FEATURE [Part::FeaturePython] newPCB  label="Pcb"  # a2plus imported part (geometry in sourceFile) (typed FeaturePython)
  fixedPosition = true
FEATURE [App::DocumentObjectGroup] Fuseholder_Schruter_FUP_horiz_closed_5x20mm_or_6_3x32mm_fp  label="Fuseholder_Cylinder-5x20mm-or-6.3x32mm_Schurter_FUP_0031.25x0_Horizontal_Closed_fp"
  Group = -> [Filk_lines,TopPads,BotPads,THPs,newPCB]
